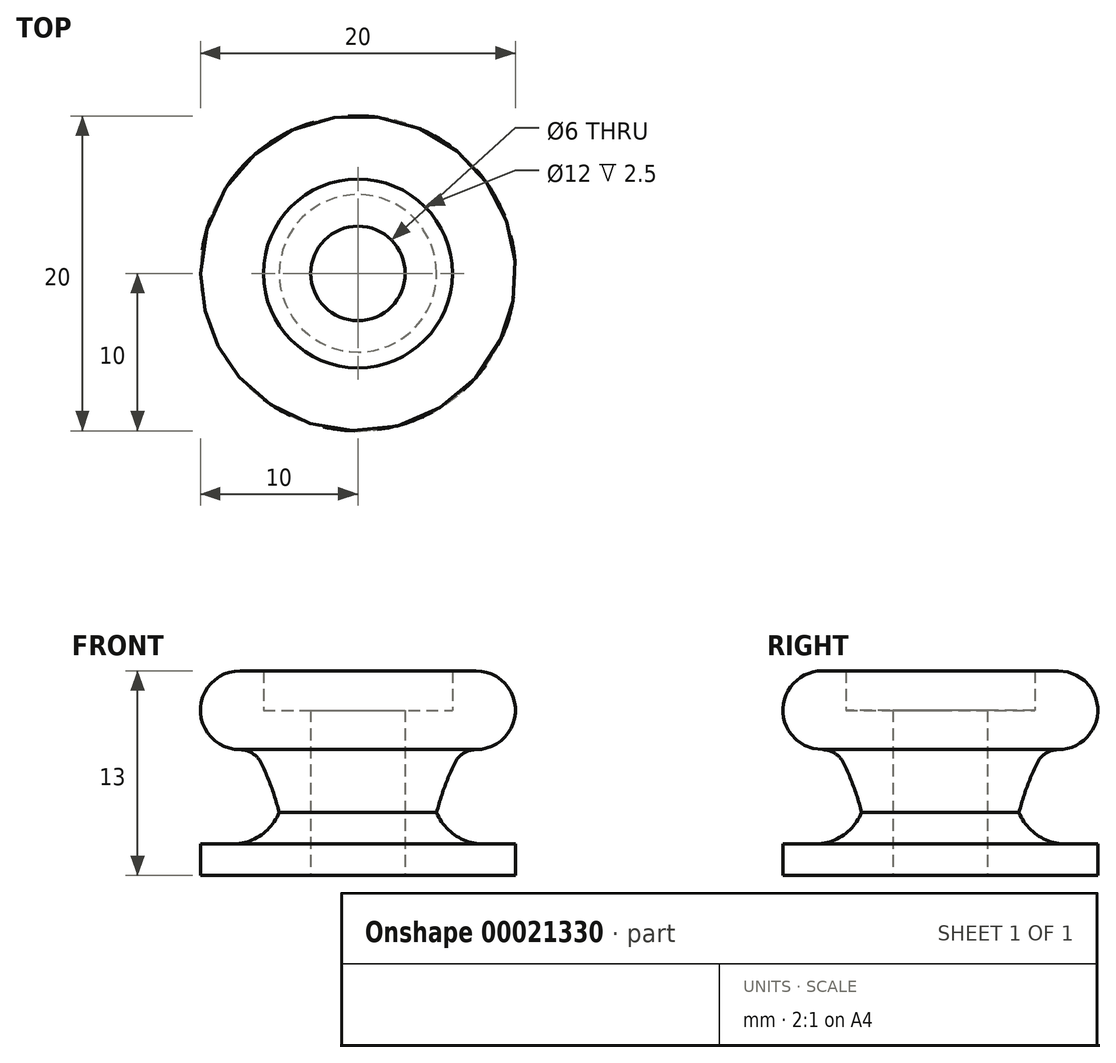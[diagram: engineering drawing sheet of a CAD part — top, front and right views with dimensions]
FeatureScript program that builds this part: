
annotation { "Feature Type Name" : "Feature", "Feature Type Description" : "" }
export const myFeature = defineFeature(function(context is Context, id is Id, definition is map)
    precondition{}
    {
        {
            var Q0;
            Q0=qCreatedBy(makeId("Front.planeOp"),FACE);
            var sketch = newSketch(context, id + "F0", { "sketchPlane" : qUnion([Q0])});
            skLineSegment(sketch, "E0", {"start": v(-3, 0) * mm, "end": v(-10, 0) * mm});
            skLineSegment(sketch, "E1", {"start": v(-10, 0) * mm, "end": v(-10, 2) * mm});
            skLineSegment(sketch, "E2", {"start": v(-10, 2) * mm, "end": v(-8, 2) * mm});
            skArc(sketch, "E3", {"start": v(-7.5, 13) * mm, "mid": v(-10, 10.5) * mm, "end": v(-7.5, 8) * mm});
            skLineSegment(sketch, "E4", {"start": v(-7.5, 13) * mm, "end": v(-6, 13) * mm});
            skLineSegment(sketch, "E5", {"start": v(-6, 13) * mm, "end": v(-6, 10.5) * mm});
            skLineSegment(sketch, "E6", {"start": v(-6, 10.5) * mm, "end": v(-3, 10.5) * mm});
            skLineSegment(sketch, "E7", {"start": v(-3, 10.5) * mm, "end": v(-3, 0) * mm});
            skLineSegment(sketch, "E8", {"start": v(0, 0) * mm, "end": v(0, 10.5) * mm, "construction": true});
            skPoint(sketch, "E9", {"position": v(-10, 10.5) * mm});
            skArc(sketch, "E10", {"start": v(-8, 2) * mm, "mid": v(-6.2, 2.55) * mm, "end": v(-5, 4) * mm});
            skArc(sketch, "E11", {"start": v(-5, 4) * mm, "mid": v(-5.5, 5.6) * mm, "end": v(-6.15, 7.16) * mm});
            skLineSegment(sketch, "E12", {"start": v(-5, 4) * mm, "end": v(-4, 0) * mm, "construction": true});
            skArc(sketch, "E13", {"start": v(-6.15, 7.16) * mm, "mid": v(-6.7, 7.77) * mm, "end": v(-7.5, 8) * mm});
            skSolve(sketch);
        }
        {
            var Q0;
            Q0=makeQuery(id+"F0.imprint","IMPRINT",FACE,{"disambiguationData":[TD([[makeQuery(id+"F0.imprint","IMPRINT",EDGE,{"derivedFrom":sQuery(id+"F0.wireOp",EDGE,"E0")}),-1.0]])]});
            var Q1;
            Q1=sQuery(id+"F0.wireOp",EDGE,"E8");
            revolve(context, id + "F1", {"entities" : qUnion([Q0]), "axis" : qUnion([Q1]), "revolveType" : RevolveType.FULL});
        }
    });
